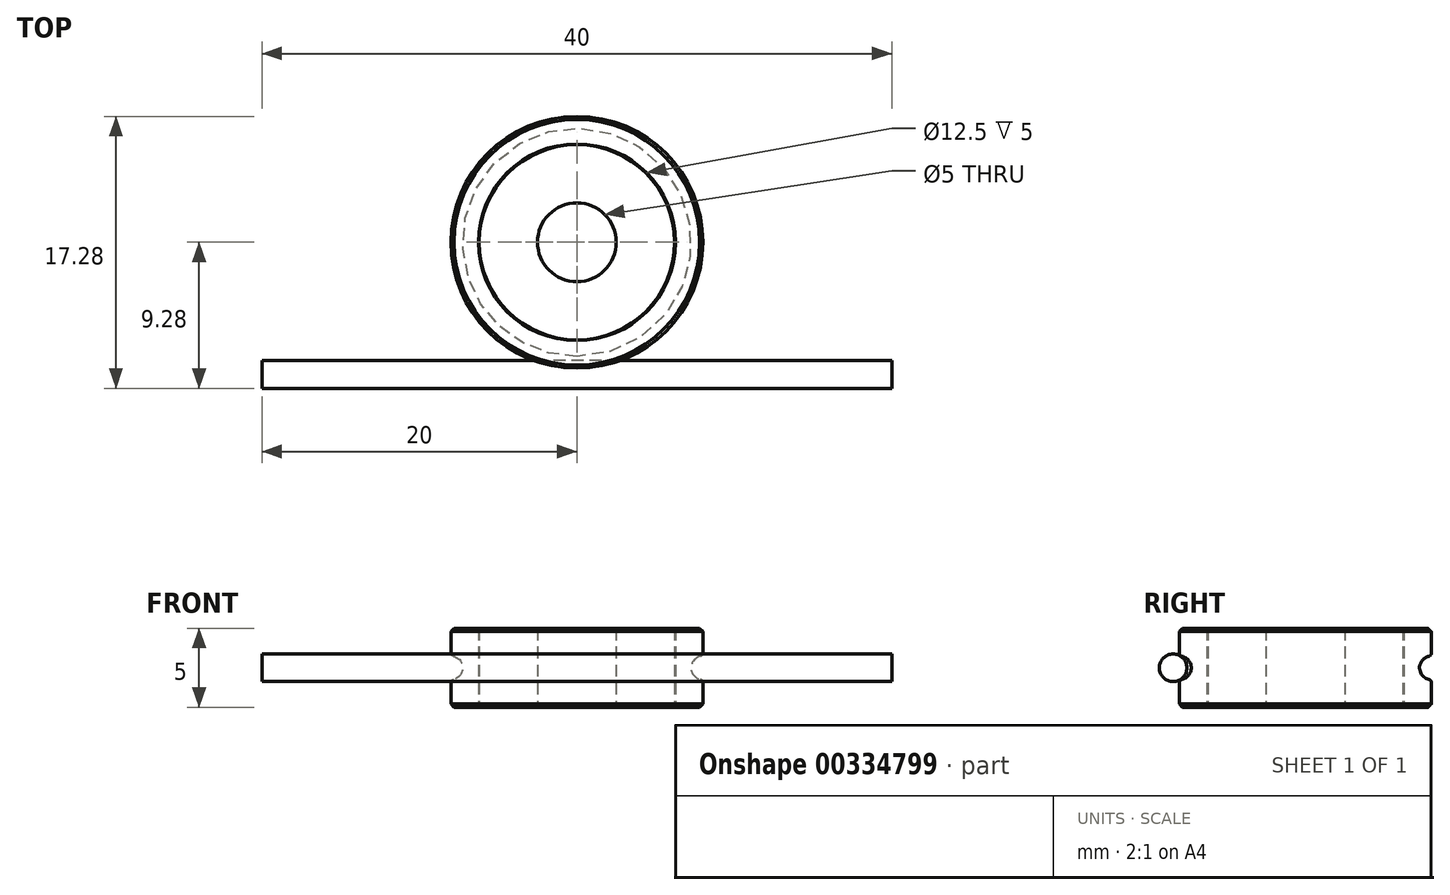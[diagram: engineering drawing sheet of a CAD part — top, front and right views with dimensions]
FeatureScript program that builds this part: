
annotation { "Feature Type Name" : "Feature", "Feature Type Description" : "" }
export const myFeature = defineFeature(function(context is Context, id is Id, definition is map)
    precondition{}
    {
        {
            var Q0;
            Q0=qCreatedBy(makeId("Top.planeOp"),FACE);
            var sketch = newSketch(context, id + "F0", { "sketchPlane" : qUnion([Q0])});
            skCircle(sketch, "E0", {"center": v(0, 0) * mm, "radius": 2.5 * mm});
            skCircle(sketch, "E1", {"center": v(0, 0) * mm, "radius": 6.2 * mm});
            skSolve(sketch);
        }
        {
            var Q0;
            Q0 = qSketchRegion(id + "F0", true);
            extrude(context, id + "F1", {"entities" : qUnion([Q0]), "depth" : 5 * mm});
        }
        {
            var Q0;
            Q0=qCreatedBy(makeId("Front.planeOp"),FACE);
            var sketch = newSketch(context, id + "F2", { "sketchPlane" : qUnion([Q0])});
            skLineSegment(sketch, "E2.top", {"start": v(-8, 0) * mm, "end": v(-6.25, 0) * mm});
            skLineSegment(sketch, "E2.left", {"start": v(-8, 5) * mm, "end": v(-8, 3.43) * mm});
            skLineSegment(sketch, "E2.right", {"start": v(-6.25, 5) * mm, "end": v(-6.25, 0) * mm});
            skArc(sketch, "E3", {"start": v(-7.84, 1.77) * mm, "mid": v(-7.25, 2.5) * mm, "end": v(-7.84, 3.23) * mm});
            skLineSegment(sketch, "E4.trimOffspring", {"start": v(-8, 1.57) * mm, "end": v(-8, 0) * mm});
            skPoint(sketch, "E5.visualSharp", {"position": v(-8, 1.75) * mm});
            skArc(sketch, "E5.filletArc", {"start": v(-7.84, 1.77) * mm, "mid": v(-7.96, 1.7) * mm, "end": v(-8, 1.57) * mm});
            skPoint(sketch, "E6.visualSharp", {"position": v(-8, 3.25) * mm});
            skArc(sketch, "E6.filletArc", {"start": v(-8, 3.43) * mm, "mid": v(-7.96, 3.3) * mm, "end": v(-7.84, 3.23) * mm});
            skLineSegment(sketch, "E7", {"start": v(0, 0) * mm, "end": v(0, 6.29) * mm, "construction": true});
            skCircle(sketch, "E8", {"center": v(-8.4, 2.5) * mm, "radius": 0.88 * mm});
            skLineSegment(sketch, "E9", {"start": v(-8, 5) * mm, "end": v(-6.25, 5) * mm});
            skSolve(sketch);
        }
        {
            var Q0;
            Q0=makeQuery(id+"F2.imprint","IMPRINT",FACE,{"disambiguationData":[TD([[makeQuery(id+"F2.imprint","IMPRINT",EDGE,{"derivedFrom":sQuery(id+"F2.wireOp",EDGE,"E2.top")}),1.0]])]});
            var Q1;
            Q1=sQuery(id+"F2.wireOp",EDGE,"E7");
            revolve(context, id + "F3", {"entities" : qUnion([Q0]), "axis" : qUnion([Q1]), "revolveType" : RevolveType.FULL});
        }
        {
            var Q0;
            Q0=makeQuery(id+"F3.opRevolve","SWEPT_EDGE",EDGE,{"disambiguationData":[OSD([sQuery(id+"F2.wireOp",EDGE,"E2.bottom"),sQuery(id+"F2.wireOp",EDGE,"E2.left")])]});
            var Q1;
            Q1=makeQuery(id+"F3.opRevolve","SWEPT_EDGE",EDGE,{"disambiguationData":[OSD([sQuery(id+"F2.wireOp",EDGE,"E2.top"),sQuery(id+"F2.wireOp",EDGE,"E4.trimOffspring")])]});
            chamfer(context, id + "F4", {"entities" : qUnion([Q0, Q1]), "width" : 0.2 * mm, "tangentPropagation" : true});
        }
        {
            var Q0;
            Q0=makeQuery(id+"F2.imprint","IMPRINT",FACE,{"disambiguationData":[TD([[makeQuery(id+"F2.imprint","IMPRINT",EDGE,{"derivedFrom":sQuery(id+"F2.wireOp",EDGE,"E8")}),1.0]])]});
            extrude(context, id + "F5", {"entities" : qUnion([Q0]), "depth" : 40 * mm, "hasSecondDirection" : true, "secondDirectionOppositeDirection" : true, "secondDirectionDepth" : 30 * mm, "symmetric" : true});
        }
        {
            var Q0;
            Q0=makeQuery(id+"F1.opExtrude","SWEPT_BODY",BODY,{"disambiguationData":[OSD([sQuery(id+"F0.wireOp",EDGE,"E0"),sQuery(id+"F0.wireOp",EDGE,"E1")])]});
            var Q1;
            Q1=makeQuery(id+"F3.opRevolve","SWEPT_BODY",BODY,{"disambiguationData":[OSD([sQuery(id+"F2.wireOp",EDGE,"E2.top"),sQuery(id+"F2.wireOp",EDGE,"E2.left"),sQuery(id+"F2.wireOp",EDGE,"E2.right"),sQuery(id+"F2.wireOp",EDGE,"E3"),sQuery(id+"F2.wireOp",EDGE,"E4.trimOffspring"),sQuery(id+"F2.wireOp",EDGE,"E5.filletArc"),sQuery(id+"F2.wireOp",EDGE,"E6.filletArc"),sQuery(id+"F2.wireOp",EDGE,"E9")])]});
            var Q2;
            Q2=makeQuery(id+"F5.opExtrude","SWEPT_BODY",BODY,{"disambiguationData":[OSD([sQuery(id+"F2.wireOp",EDGE,"E8")])]});
            var Q3;
            Q3=sQuery(id+"F0.wireOp",EDGE,"E0");
            transform(context, id + "F6", {"entities" : qUnion([Q0, Q1, Q2]), "transformType" : TransformType.ROTATION, "transformAxis" : qUnion([Q3]), "angle" : 90 * degree, "makeCopy" : false});
        }
    });
